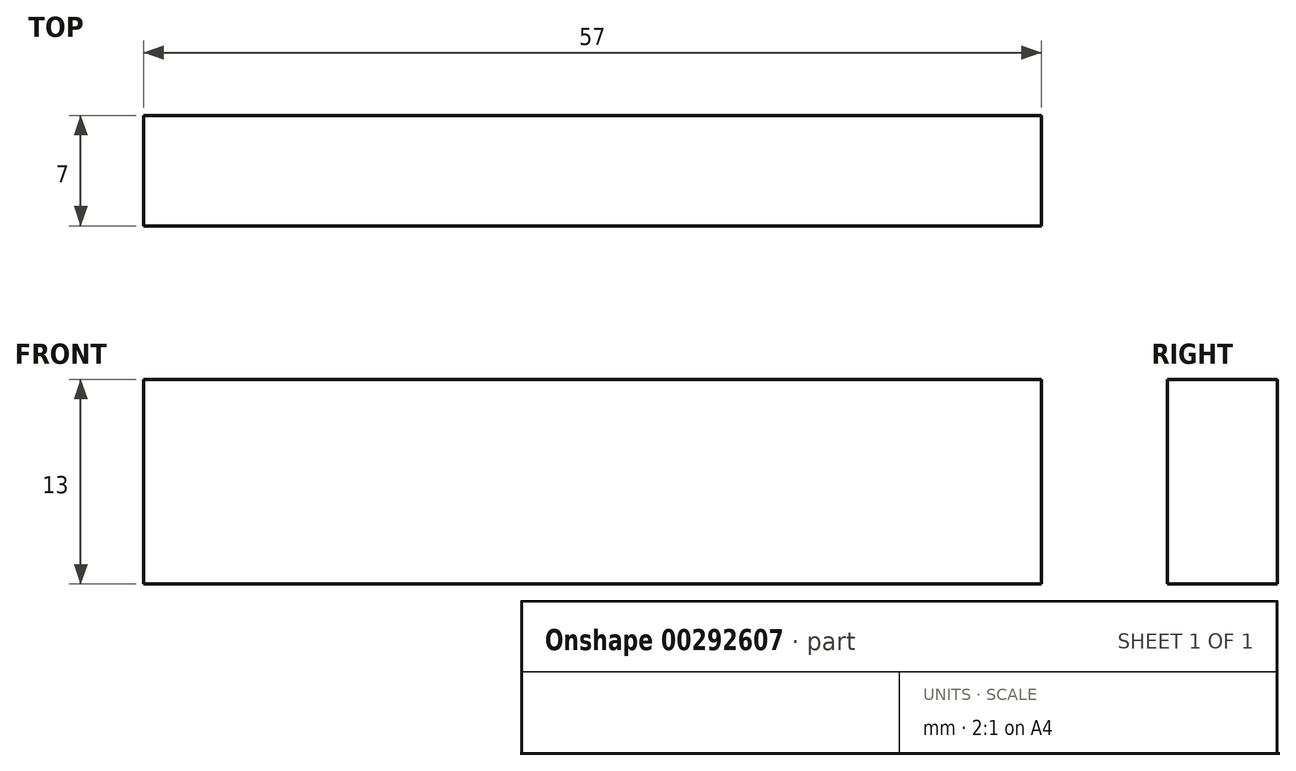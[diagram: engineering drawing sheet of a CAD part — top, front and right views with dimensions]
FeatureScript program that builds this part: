
annotation { "Feature Type Name" : "Feature", "Feature Type Description" : "" }
export const myFeature = defineFeature(function(context is Context, id is Id, definition is map)
    precondition{}
    {
        {
            var Q0;
            Q0=qCreatedBy(makeId("Front.planeOp"),FACE);
            var sketch = newSketch(context, id + "F0", { "sketchPlane" : qUnion([Q0])});
            skLineSegment(sketch, "E0.bottom", {"start": v(0, 13) * mm, "end": v(57, 13) * mm});
            skLineSegment(sketch, "E0.top", {"start": v(0, 0) * mm, "end": v(57, 0) * mm});
            skLineSegment(sketch, "E0.left", {"start": v(0, 13) * mm, "end": v(0, 0) * mm});
            skLineSegment(sketch, "E0.right", {"start": v(57, 13) * mm, "end": v(57, 0) * mm});
            skSolve(sketch);
        }
        {
            var Q0;
            Q0=makeQuery(id+"F0.imprint","IMPRINT",FACE,{"disambiguationData":[TD([[makeQuery(id+"F0.imprint","IMPRINT",EDGE,{"derivedFrom":sQuery(id+"F0.wireOp",EDGE,"E0.bottom")}),-1.0]])]});
            extrude(context, id + "F1", {"entities" : qUnion([Q0]), "depth" : 7 * mm});
        }
    });
